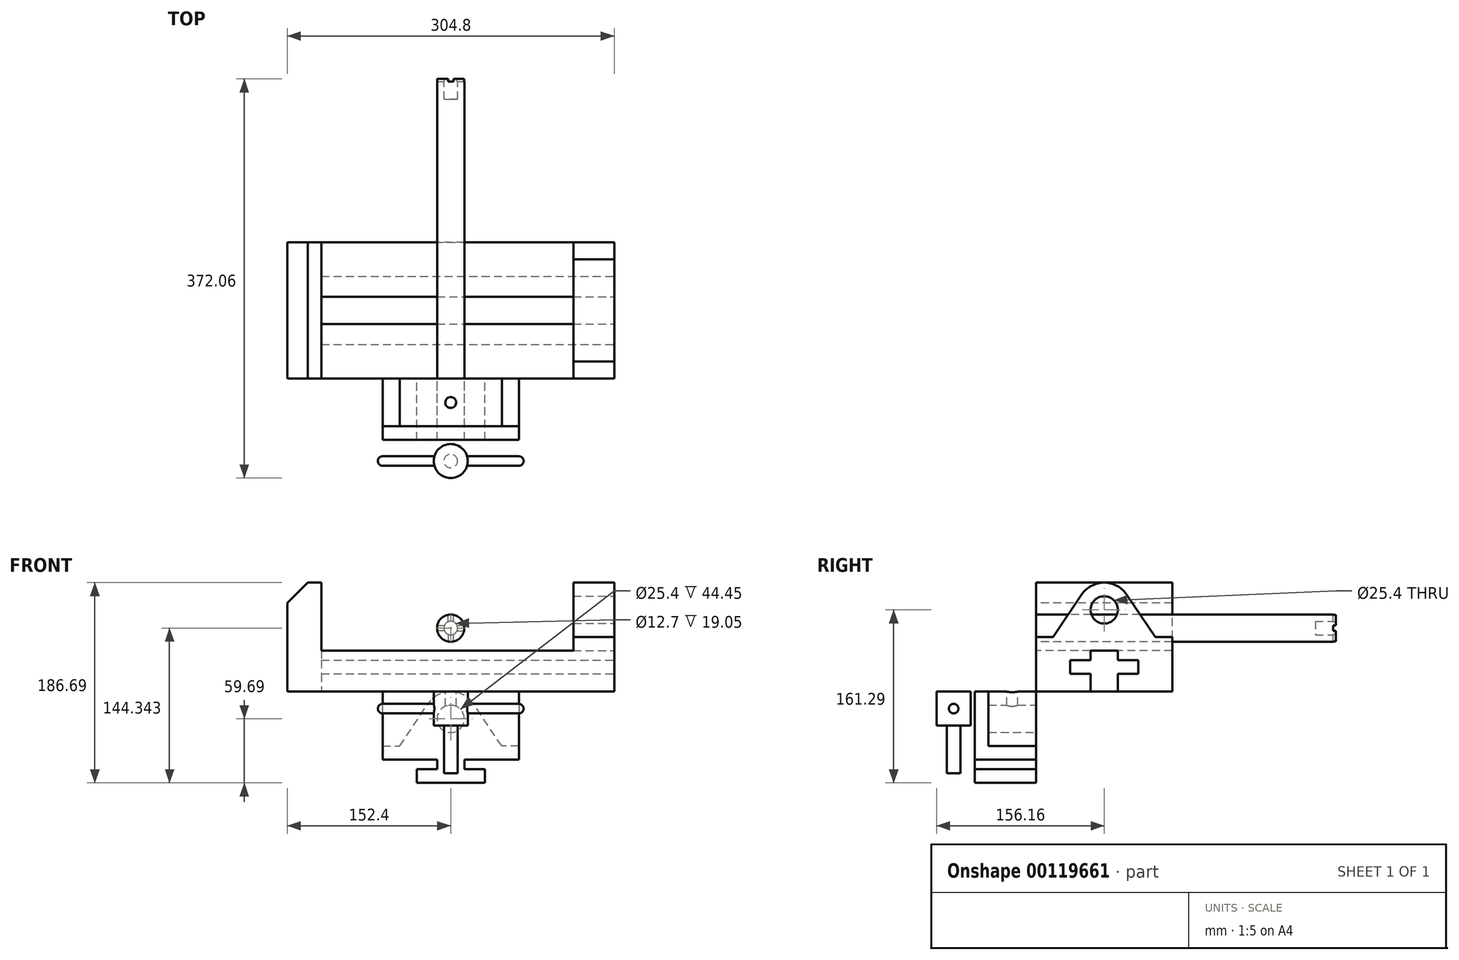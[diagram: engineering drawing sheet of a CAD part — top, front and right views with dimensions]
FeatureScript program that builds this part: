
annotation { "Feature Type Name" : "Feature", "Feature Type Description" : "" }
export const myFeature = defineFeature(function(context is Context, id is Id, definition is map)
    precondition{}
    {
        {
            var Q0;
            Q0=qCreatedBy(makeId("Front.planeOp"),FACE);
            var sketch = newSketch(context, id + "F0", { "sketchPlane" : qUnion([Q0])});
            skLineSegment(sketch, "E0", {"start": v(-152.4, 0) * mm, "end": v(152.4, 0) * mm});
            skLineSegment(sketch, "E1", {"start": v(152.4, 0) * mm, "end": v(152.4, 101.6) * mm});
            skLineSegment(sketch, "E2", {"start": v(152.4, 101.6) * mm, "end": v(114.3, 101.6) * mm});
            skLineSegment(sketch, "E3", {"start": v(114.3, 101.6) * mm, "end": v(114.3, 38.1) * mm});
            skLineSegment(sketch, "E4", {"start": v(114.3, 38.1) * mm, "end": v(-120.65, 38.1) * mm});
            skLineSegment(sketch, "E5", {"start": v(-120.65, 38.1) * mm, "end": v(-120.65, 101.6) * mm});
            skLineSegment(sketch, "E6", {"start": v(-120.65, 101.6) * mm, "end": v(-133.35, 101.6) * mm});
            skLineSegment(sketch, "E7", {"start": v(-133.35, 101.6) * mm, "end": v(-152.4, 82.55) * mm});
            skLineSegment(sketch, "E8", {"start": v(-152.4, 82.55) * mm, "end": v(-152.4, 0) * mm});
            skSolve(sketch);
        }
        {
            var Q0;
            Q0=makeQuery(id+"F0.imprint","IMPRINT",FACE,{"disambiguationData":[TD([[makeQuery(id+"F0.imprint","IMPRINT",EDGE,{"derivedFrom":sQuery(id+"F0.wireOp",EDGE,"E0")}),1.0]])]});
            extrude(context, id + "F1", {"entities" : qUnion([Q0]), "oppositeDirection" : true, "depth" : 127 * mm});
        }
        {
            var Q0;
            Q0=makeQuery(id+"F1.opExtrude","SWEPT_FACE",FACE,{"disambiguationData":[OSD([sQuery(id+"F0.wireOp",EDGE,"E1")])]});
            var sketch = newSketch(context, id + "F2", { "sketchPlane" : qUnion([Q0])});
            skLineSegment(sketch, "E9", {"start": v(0, 0) * mm, "end": v(0, 50.8) * mm});
            skLineSegment(sketch, "E10", {"start": v(0, 50.8) * mm, "end": v(15.87, 50.8) * mm});
            skLineSegment(sketch, "E11", {"start": v(15.87, 50.8) * mm, "end": v(42.4, 90.35) * mm});
            skLineSegment(sketch, "E12", {"start": v(0, 0) * mm, "end": v(50.8, 0) * mm});
            skLineSegment(sketch, "E13", {"start": v(50.8, 0) * mm, "end": v(50.8, 16.51) * mm});
            skLineSegment(sketch, "E14", {"start": v(50.8, 16.51) * mm, "end": v(31.75, 16.51) * mm});
            skLineSegment(sketch, "E15", {"start": v(31.75, 16.51) * mm, "end": v(31.75, 29.21) * mm});
            skLineSegment(sketch, "E16", {"start": v(31.75, 29.21) * mm, "end": v(50.8, 29.21) * mm});
            skLineSegment(sketch, "E17", {"start": v(50.8, 29.21) * mm, "end": v(50.8, 38.1) * mm});
            skLineSegment(sketch, "E18", {"start": v(50.8, 38.1) * mm, "end": v(76.2, 38.1) * mm});
            skLineSegment(sketch, "E19", {"start": v(76.2, 38.1) * mm, "end": v(76.2, 29.21) * mm});
            skLineSegment(sketch, "E20", {"start": v(76.2, 29.21) * mm, "end": v(95.25, 29.21) * mm});
            skLineSegment(sketch, "E21", {"start": v(95.25, 29.21) * mm, "end": v(95.25, 16.51) * mm});
            skLineSegment(sketch, "E22", {"start": v(95.25, 16.51) * mm, "end": v(76.2, 16.51) * mm});
            skLineSegment(sketch, "E23", {"start": v(76.2, 16.51) * mm, "end": v(76.2, 0) * mm});
            skLineSegment(sketch, "E24", {"start": v(50.8, 0) * mm, "end": v(127, 0) * mm});
            skLineSegment(sketch, "E25", {"start": v(127, 0) * mm, "end": v(127, 50.8) * mm});
            skArc(sketch, "E26", {"start": v(42.4, 90.35) * mm, "mid": v(63.5, 101.6) * mm, "end": v(84.6, 90.35) * mm});
            skLineSegment(sketch, "E27", {"start": v(63.5, 101.6) * mm, "end": v(63.5, 0) * mm, "construction": true});
            skLineSegment(sketch, "E28", {"start": v(63.5, 76.2) * mm, "end": v(0, 76.2) * mm, "construction": true});
            skLineSegment(sketch, "E29", {"start": v(63.5, 76.2) * mm, "end": v(127, 76.2) * mm, "construction": true});
            skCircle(sketch, "E30", {"center": v(63.5, 76.2) * mm, "radius": 12.7 * mm});
            skLineSegment(sketch, "E31", {"start": v(127, 50.8) * mm, "end": v(111.13, 50.8) * mm});
            skLineSegment(sketch, "E32", {"start": v(84.6, 90.35) * mm, "end": v(111.13, 50.8) * mm});
            skSolve(sketch);
        }
        {
            var Q0;
            {var subQ4=sQuery(id+"F2.wireOp",EDGE,"E10");Q0=makeQuery(id+"F2.imprint","IMPRINT",FACE,{"disambiguationData":[TD([[makeQuery(id+"F2.imprint","IMPRINT",EDGE,{"derivedFrom":subQ4}),1.0]])]});}
            var Q1;
            {var subQ4=sQuery(id+"F2.wireOp",EDGE,"E31");Q1=makeQuery(id+"F2.imprint","IMPRINT",FACE,{"disambiguationData":[TD([[makeQuery(id+"F2.imprint","IMPRINT",EDGE,{"derivedFrom":subQ4}),-1.0]])]});}
            var Q2;
            Q2=makeQuery(id+"F2.imprint","IMPRINT",FACE,{"disambiguationData":[TD([[makeQuery(id+"F2.imprint","IMPRINT",EDGE,{"derivedFrom":sQuery(id+"F2.wireOp",EDGE,"E30")}),1.0]])]});
            extrude(context, id + "F3", {"entities" : qUnion([Q0, Q1, Q2]), "operationType" : NewBodyOperationType.REMOVE, "endBound" : BoundingType.UP_TO_NEXT, "oppositeDirection" : true, "depth" : 25.4 * mm});
        }
        {
            var Q0;
            {var subQ1=sQuery(id+"F2.wireOp",EDGE,"E13");Q0=makeQuery(id+"F2.imprint","IMPRINT",FACE,{"disambiguationData":[TD([[makeQuery(id+"F2.imprint","IMPRINT",EDGE,{"derivedFrom":subQ1}),-1.0]])]});}
            var Q1;
            Q1=makeQuery(id+"F1.opExtrude","SWEPT_FACE",FACE,{"disambiguationData":[OSD([sQuery(id+"F0.wireOp",EDGE,"E5")])]});
            extrude(context, id + "F4", {"entities" : qUnion([Q0]), "operationType" : NewBodyOperationType.REMOVE, "endBound" : BoundingType.UP_TO_SURFACE, "oppositeDirection" : true, "endBoundEntityFace" : qUnion([Q1]), "depth" : 25.4 * mm});
        }
        {
            var Q0;
            Q0=qCreatedBy(makeId("Front.planeOp"),FACE);
            var sketch = newSketch(context, id + "F5", { "sketchPlane" : qUnion([Q0])});
            skLineSegment(sketch, "E33", {"start": v(-63.5, -63.5) * mm, "end": v(-12.7, -63.5) * mm});
            skLineSegment(sketch, "E34", {"start": v(-12.7, -63.5) * mm, "end": v(-12.7, -72.4) * mm});
            skLineSegment(sketch, "E35", {"start": v(-12.7, -72.4) * mm, "end": v(-31.75, -72.4) * mm});
            skLineSegment(sketch, "E36", {"start": v(-31.75, -72.4) * mm, "end": v(-31.75, -85.1) * mm});
            skLineSegment(sketch, "E37", {"start": v(-31.75, -85.1) * mm, "end": v(31.75, -85.1) * mm});
            skLineSegment(sketch, "E38", {"start": v(31.75, -85.1) * mm, "end": v(31.75, -72.4) * mm});
            skLineSegment(sketch, "E39", {"start": v(12.7, -72.4) * mm, "end": v(31.75, -72.4) * mm});
            skLineSegment(sketch, "E40", {"start": v(12.7, -72.4) * mm, "end": v(12.7, -63.5) * mm});
            skLineSegment(sketch, "E41", {"start": v(12.7, -63.5) * mm, "end": v(63.5, -63.5) * mm});
            skLineSegment(sketch, "E42", {"start": v(63.5, -63.5) * mm, "end": v(63.5, -50.8) * mm});
            skLineSegment(sketch, "E43", {"start": v(63.5, -50.8) * mm, "end": v(47.63, -50.8) * mm});
            skLineSegment(sketch, "E44", {"start": v(47.63, -50.8) * mm, "end": v(21.1, -11.25) * mm});
            skLineSegment(sketch, "E45", {"start": v(-63.5, -63.5) * mm, "end": v(-63.5, -50.8) * mm});
            skLineSegment(sketch, "E46", {"start": v(-63.5, -50.8) * mm, "end": v(-47.62, -50.8) * mm});
            skLineSegment(sketch, "E47", {"start": v(-47.62, -50.8) * mm, "end": v(-21.1, -11.25) * mm});
            skArc(sketch, "E48", {"start": v(-21.1, -11.25) * mm, "mid": v(0, 0) * mm, "end": v(21.1, -11.25) * mm});
            skCircle(sketch, "E49", {"center": v(0, -25.4) * mm, "radius": 12.7 * mm});
            skLineSegment(sketch, "E50", {"start": v(-63.5, -50.8) * mm, "end": v(-63.5, 0) * mm});
            skLineSegment(sketch, "E51", {"start": v(-63.5, 0) * mm, "end": v(63.5, 0) * mm});
            skLineSegment(sketch, "E52", {"start": v(63.5, 0) * mm, "end": v(63.5, -63.5) * mm});
            skLineSegment(sketch, "E53", {"start": v(0, 0) * mm, "end": v(0, -85.1) * mm, "construction": true});
            skSolve(sketch);
        }
        {
            var Q0;
            Q0 = qSketchRegion(id + "F5", true);
            var Q1;
            Q1=makeQuery(id+"F5.imprint","IMPRINT",FACE,{"disambiguationData":[TD([[makeQuery(id+"F5.imprint","IMPRINT",EDGE,{"derivedFrom":sQuery(id+"F5.wireOp",EDGE,"E49")}),1.0]])]});
            extrude(context, id + "F6", {"entities" : qUnion([Q0, Q1]), "depth" : 57.15 * mm});
        }
        {
            var Q0;
            Q0=makeQuery(id+"F6.opExtrude","SWEPT_FACE",FACE,{"disambiguationData":[OSD([sQuery(id+"F5.wireOp",EDGE,"E51")])]});
            var sketch = newSketch(context, id + "F7", { "sketchPlane" : qUnion([Q0])});
            skCircle(sketch, "E54", {"center": v(0, -22.23) * mm, "radius": 5.08 * mm});
            skSolve(sketch);
        }
        {
            var Q0;
            Q0 = qSketchRegion(id + "F7", true);
            extrude(context, id + "F8", {"entities" : qUnion([Q0]), "operationType" : NewBodyOperationType.REMOVE, "oppositeDirection" : true, "depth" : 31.75 * mm});
        }
        {
            var Q0;
            {var subQ6=sQuery(id+"F5.wireOp",EDGE,"E43");Q0=makeQuery(id+"F5.imprint","IMPRINT",FACE,{"disambiguationData":[TD([[makeQuery(id+"F5.imprint","IMPRINT",EDGE,{"derivedFrom":subQ6}),-1.0]])]});}
            var Q1;
            Q1=makeQuery(id+"F5.imprint","IMPRINT",FACE,{"disambiguationData":[TD([[makeQuery(id+"F5.imprint","IMPRINT",EDGE,{"derivedFrom":sQuery(id+"F5.wireOp",EDGE,"E46")}),1.0]])]});
            extrude(context, id + "F9", {"entities" : qUnion([Q0, Q1]), "operationType" : NewBodyOperationType.REMOVE, "depth" : 44.45 * mm});
        }
        {
            var Q0;
            Q0=makeQuery(id+"F5.imprint","IMPRINT",FACE,{"disambiguationData":[TD([[makeQuery(id+"F5.imprint","IMPRINT",EDGE,{"derivedFrom":sQuery(id+"F5.wireOp",EDGE,"E49")}),1.0]])]});
            extrude(context, id + "F10", {"entities" : qUnion([Q0]), "operationType" : NewBodyOperationType.REMOVE, "depth" : 44.45 * mm});
        }
        {
            var Q0;
            Q0=qCreatedBy(makeId("Front.planeOp"),FACE);
            var sketch = newSketch(context, id + "F11", { "sketchPlane" : qUnion([Q0])});
            skCircle(sketch, "E55", {"center": v(0, 59.25) * mm, "radius": 12.7 * mm});
            skSolve(sketch);
        }
        {
            var Q0;
            Q0=makeQuery(id+"F11.imprint","IMPRINT",FACE,{"disambiguationData":[TD([[makeQuery(id+"F11.imprint","IMPRINT",EDGE,{"derivedFrom":sQuery(id+"F11.wireOp",EDGE,"E55")}),1.0]])]});
            var Q1;
            Q1=sQuery(id+"F11.wireOp",EDGE,"E55");
            extrude(context, id + "F12", {"entities" : qUnion([Q0]), "surfaceEntities" : qUnion([Q1]), "oppositeDirection" : true, "depth" : 279.4 * mm});
        }
        {
            var Q0;
            Q0=makeQuery(id+"F12.opExtrude","CAP_FACE",FACE,{"disambiguationData":[OSD([sQuery(id+"F11.wireOp",EDGE,"E55")])],"isStart":false});
            var sketch = newSketch(context, id + "F13", { "sketchPlane" : qUnion([Q0])});
            skCircle(sketch, "E56", {"center": v(0, 59.25) * mm, "radius": 6.35 * mm});
            skLineSegment(sketch, "E57", {"start": v(0, 46.55) * mm, "end": v(0, 71.95) * mm, "construction": true});
            skLineSegment(sketch, "E58", {"start": v(12.7, 59.25) * mm, "end": v(-12.7, 59.25) * mm, "construction": true});
            skLineSegment(sketch, "E59", {"start": v(2.54, 53.43) * mm, "end": v(2.54, 46.8) * mm});
            skLineSegment(sketch, "E60", {"start": v(-2.54, 46.8) * mm, "end": v(-2.54, 53.43) * mm});
            skLineSegment(sketch, "E61", {"start": v(12.44, 61.8) * mm, "end": v(5.82, 61.8) * mm});
            skLineSegment(sketch, "E62", {"start": v(5.82, 56.71) * mm, "end": v(12.44, 56.71) * mm});
            skLineSegment(sketch, "E63", {"start": v(-5.82, 56.71) * mm, "end": v(-12.44, 56.71) * mm});
            skPoint(sketch, "E63.startSnap0", {"position": v(9.13, 56.71) * mm});
            skLineSegment(sketch, "E64", {"start": v(-5.82, 61.8) * mm, "end": v(-12.44, 61.8) * mm});
            skLineSegment(sketch, "E65", {"start": v(2.54, 65.07) * mm, "end": v(2.54, 71.7) * mm});
            skLineSegment(sketch, "E66", {"start": v(-2.54, 65.07) * mm, "end": v(-2.54, 71.7) * mm});
            skSolve(sketch);
        }
        {
            var Q0;
            Q0 = qSketchRegion(id + "F13", true);
            extrude(context, id + "F14", {"entities" : qUnion([Q0]), "operationType" : NewBodyOperationType.REMOVE, "oppositeDirection" : true, "depth" : 19.05 * mm});
        }
        {
            var Q0;
            {var subQ0=sQuery(id+"F13.wireOp",EDGE,"E61");Q0=makeQuery(id+"F13.imprint","IMPRINT",FACE,{"disambiguationData":[TD([[makeQuery(id+"F13.imprint","IMPRINT",EDGE,{"derivedFrom":subQ0}),1.0]])]});}
            var Q1;
            {var subQ0=sQuery(id+"F13.wireOp",EDGE,"E59");Q1=makeQuery(id+"F13.imprint","IMPRINT",FACE,{"disambiguationData":[TD([[makeQuery(id+"F13.imprint","IMPRINT",EDGE,{"derivedFrom":subQ0}),-1.0]])]});}
            var Q2;
            {var subQ0=sQuery(id+"F13.wireOp",EDGE,"E63");Q2=makeQuery(id+"F13.imprint","IMPRINT",FACE,{"disambiguationData":[TD([[makeQuery(id+"F13.imprint","IMPRINT",EDGE,{"derivedFrom":subQ0}),-1.0]])]});}
            var Q3;
            {var subQ0=sQuery(id+"F13.wireOp",EDGE,"E65");Q3=makeQuery(id+"F13.imprint","IMPRINT",FACE,{"disambiguationData":[TD([[makeQuery(id+"F13.imprint","IMPRINT",EDGE,{"derivedFrom":subQ0}),1.0]])]});}
            extrude(context, id + "F15", {"entities" : qUnion([Q0, Q1, Q2, Q3]), "operationType" : NewBodyOperationType.REMOVE, "oppositeDirection" : true, "depth" : 2.54 * mm});
        }
        {
            var Q0;
            Q0=qCreatedBy(makeId("Top.planeOp"),FACE);
            var sketch = newSketch(context, id + "F16", { "sketchPlane" : qUnion([Q0])});
            skCircle(sketch, "E67", {"center": v(0, -76.79) * mm, "radius": 15.88 * mm});
            skSolve(sketch);
        }
        {
            var Q0;
            Q0 = qSketchRegion(id + "F16", true);
            extrude(context, id + "F17", {"entities" : qUnion([Q0]), "oppositeDirection" : true, "depth" : 31.75 * mm});
        }
        {
            var Q0;
            Q0=makeQuery(id+"F17.opExtrude","CAP_FACE",FACE,{"disambiguationData":[OSD([sQuery(id+"F16.wireOp",EDGE,"E67")])],"isStart":false});
            var sketch = newSketch(context, id + "F18", { "sketchPlane" : qUnion([Q0])});
            skCircle(sketch, "E68", {"center": v(0, 76.79) * mm, "radius": 6.35 * mm});
            skSolve(sketch);
        }
        {
            var Q0;
            Q0 = qSketchRegion(id + "F18", true);
            extrude(context, id + "F19", {"entities" : qUnion([Q0]), "operationType" : NewBodyOperationType.ADD, "depth" : 44.45 * mm});
        }
        {
            var Q0;
            Q0=makeQuery(id+"F6.opExtrude","SWEPT_FACE",FACE,{"disambiguationData":[OSD([sQuery(id+"F5.wireOp",EDGE,"E52")])]});
            var sketch = newSketch(context, id + "F20", { "sketchPlane" : qUnion([Q0])});
            skCircle(sketch, "E69", {"center": v(-76.78, -15.88) * mm, "radius": 4.45 * mm});
            skSolve(sketch);
        }
        {
            var Q0;
            Q0=makeQuery(id+"F20.imprint","IMPRINT",FACE,{"disambiguationData":[TD([[makeQuery(id+"F20.imprint","IMPRINT",EDGE,{"derivedFrom":sQuery(id+"F20.wireOp",EDGE,"E69")}),1.0]])]});
            extrude(context, id + "F21", {"entities" : qUnion([Q0]), "operationType" : NewBodyOperationType.ADD, "oppositeDirection" : true, "depth" : 127 * mm});
        }
        {
            var Q0;
            Q0=makeQuery(id+"F21.opExtrude","CAP_FACE",FACE,{"disambiguationData":[OSD([sQuery(id+"F20.wireOp",EDGE,"E69")])],"isStart":true});
            var sketch = newSketch(context, id + "F22", { "sketchPlane" : qUnion([Q0])});
            skLineSegment(sketch, "E70", {"start": v(-76.78, -11.43) * mm, "end": v(-76.78, -20.32) * mm});
            skArc(sketch, "E71", {"start": v(-76.78, -20.32) * mm, "mid": v(-72.34, -15.88) * mm, "end": v(-76.78, -11.43) * mm});
            skLineSegment(sketch, "E72", {"start": v(-76.78, -11.43) * mm, "end": v(-76.78, -20.32) * mm, "construction": true});
            skSolve(sketch);
        }
        {
            var Q0;
            Q0=makeQuery(id+"F22.imprint","IMPRINT",FACE,{"disambiguationData":[TD([[makeQuery(id+"F22.imprint","IMPRINT",EDGE,{"derivedFrom":sQuery(id+"F22.wireOp",EDGE,"E70")}),1.0]])]});
            var Q1;
            Q1=sQuery(id+"F22.wireOp",EDGE,"E70");
            revolve(context, id + "F23", {"operationType" : NewBodyOperationType.ADD, "entities" : qUnion([Q0]), "axis" : qUnion([Q1]), "revolveType" : RevolveType.TWO_DIRECTIONS, "oppositeDirection" : true, "angle" : 360 * degree, "angleBack" : 360 * degree});
        }
        {
            var Q0;
            Q0=makeQuery(id+"F21.opExtrude","CAP_FACE",FACE,{"disambiguationData":[OSD([sQuery(id+"F20.wireOp",EDGE,"E69")])],"isStart":false});
            var sketch = newSketch(context, id + "F24", { "sketchPlane" : qUnion([Q0])});
            skLineSegment(sketch, "E73", {"start": v(72.34, -15.88) * mm, "end": v(81.23, -15.88) * mm});
            skArc(sketch, "E74", {"start": v(81.23, -15.88) * mm, "mid": v(76.78, -11.43) * mm, "end": v(72.34, -15.88) * mm});
            skLineSegment(sketch, "E75", {"start": v(71.35, -15.88) * mm, "end": v(82.08, -15.88) * mm, "construction": true});
            skSolve(sketch);
        }
        {
            var Q0;
            Q0=makeQuery(id+"F24.imprint","IMPRINT",FACE,{"disambiguationData":[TD([[makeQuery(id+"F24.imprint","IMPRINT",EDGE,{"derivedFrom":sQuery(id+"F24.wireOp",EDGE,"E73")}),1.0]])]});
            var Q1;
            Q1=sQuery(id+"F24.wireOp",EDGE,"E75");
            revolve(context, id + "F25", {"operationType" : NewBodyOperationType.ADD, "entities" : qUnion([Q0]), "axis" : qUnion([Q1]), "revolveType" : RevolveType.FULL});
        }
    });
